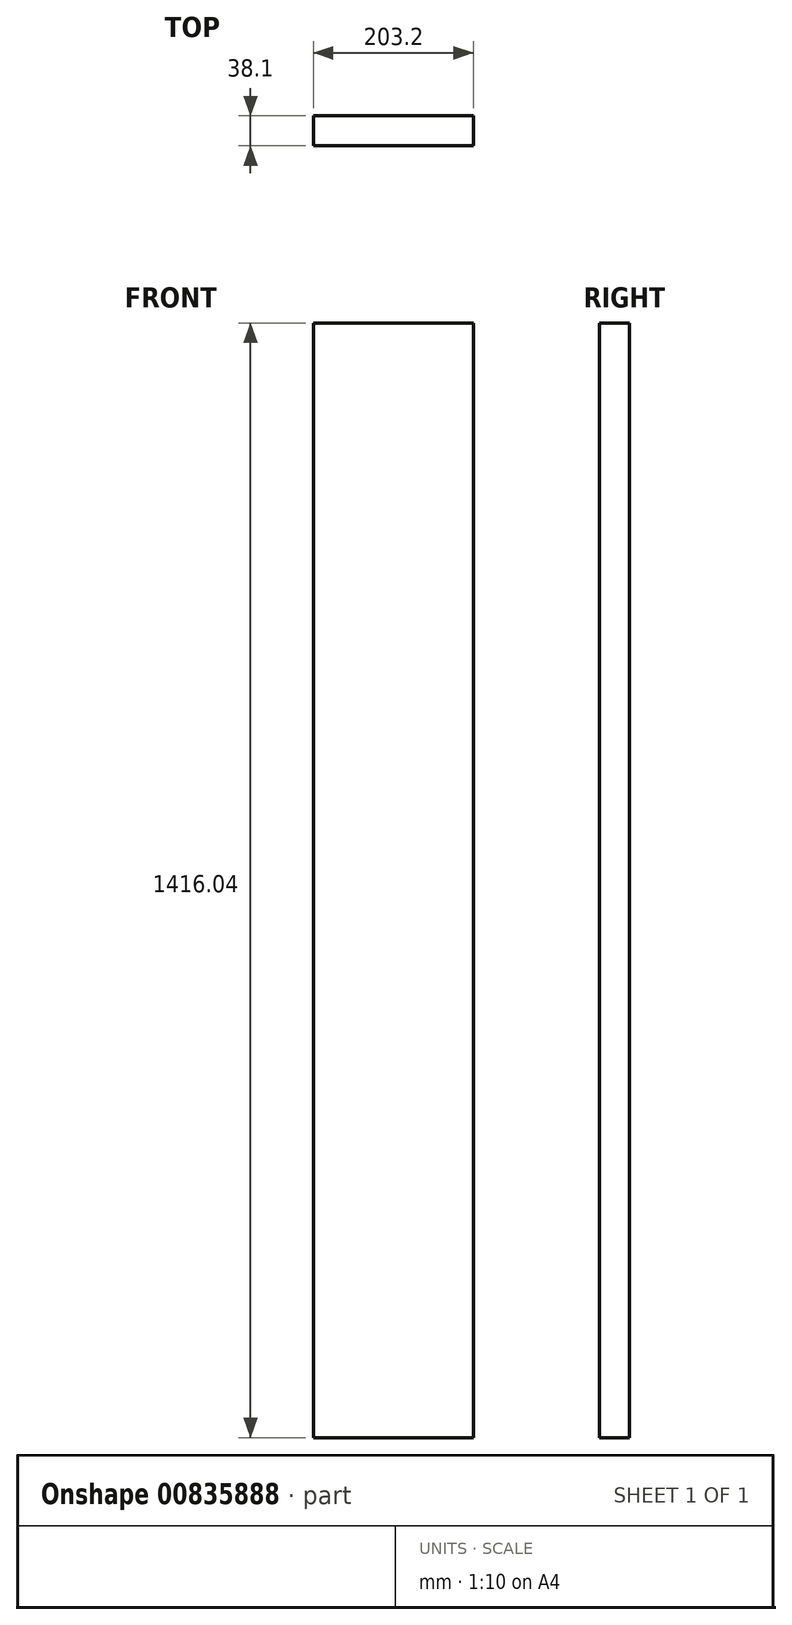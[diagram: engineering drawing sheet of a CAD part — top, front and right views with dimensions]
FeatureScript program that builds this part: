
annotation { "Feature Type Name" : "Feature", "Feature Type Description" : "" }
export const myFeature = defineFeature(function(context is Context, id is Id, definition is map)
    precondition{}
    {
        {
            var Q0;
            Q0=qCreatedBy(makeId("Front.planeOp"),FACE);
            var sketch = newSketch(context, id + "F0", { "sketchPlane" : qUnion([Q0])});
            skLineSegment(sketch, "E0.bottom", {"start": v(101.6, -708.02) * mm, "end": v(-101.6, -708.02) * mm});
            skLineSegment(sketch, "E0.top", {"start": v(101.6, 708.02) * mm, "end": v(-101.6, 708.02) * mm});
            skLineSegment(sketch, "E0.left", {"start": v(101.6, -708.02) * mm, "end": v(101.6, 708.02) * mm});
            skLineSegment(sketch, "E0.right", {"start": v(-101.6, -708.02) * mm, "end": v(-101.6, 708.02) * mm});
            skPoint(sketch, "E0.middle", {"position": v(0, 0) * mm});
            skSolve(sketch);
        }
        {
            var Q0;
            Q0 = qSketchRegion(id + "F0", true);
            extrude(context, id + "F1", {"entities" : qUnion([Q0]), "endBound" : BoundingType.SYMMETRIC, "depth" : 38.1 * mm, "offsetDistance" : 25.4 * mm});
        }
    });
